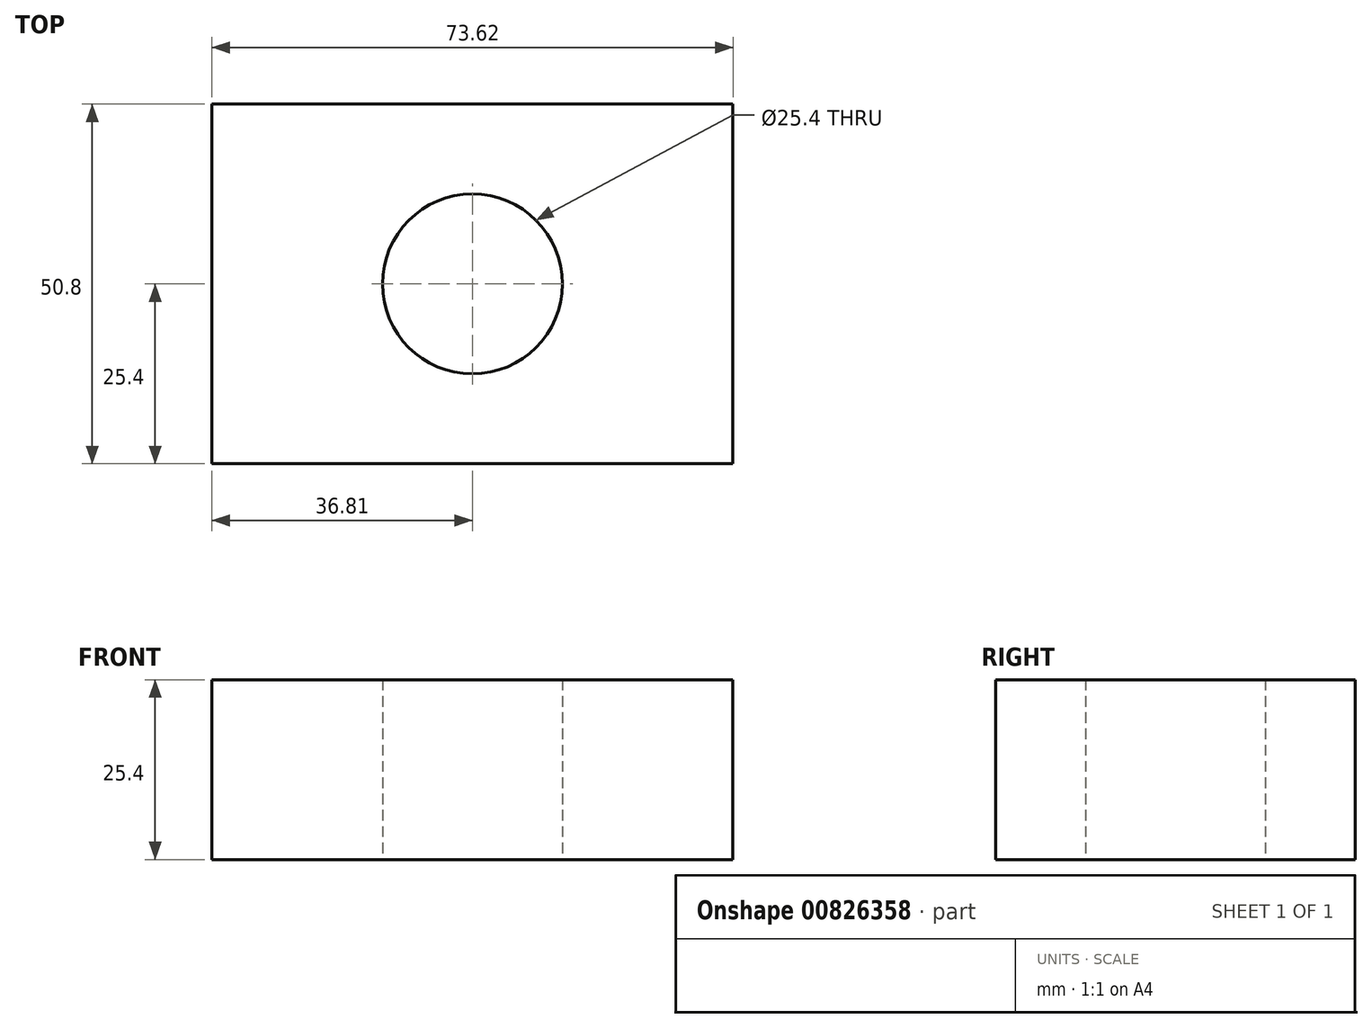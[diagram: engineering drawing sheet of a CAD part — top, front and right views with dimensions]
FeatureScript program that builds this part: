
annotation { "Feature Type Name" : "Feature", "Feature Type Description" : "" }
export const myFeature = defineFeature(function(context is Context, id is Id, definition is map)
    precondition{}
    {
        {
            var Q0;
            Q0=qCreatedBy(makeId("Top.planeOp"),FACE);
            var sketch = newSketch(context, id + "F0", { "sketchPlane" : qUnion([Q0])});
            skLineSegment(sketch, "E0.bottom", {"start": v(36.8, 25.4) * mm, "end": v(-36.8, 25.4) * mm});
            skLineSegment(sketch, "E0.top", {"start": v(36.8, -25.4) * mm, "end": v(-36.8, -25.4) * mm});
            skLineSegment(sketch, "E0.left", {"start": v(36.8, 25.4) * mm, "end": v(36.8, -25.4) * mm});
            skLineSegment(sketch, "E0.right", {"start": v(-36.8, 25.4) * mm, "end": v(-36.8, -25.4) * mm});
            skPoint(sketch, "E0.middle", {"position": v(0, 0) * mm});
            skCircle(sketch, "E1", {"center": v(0, 0) * mm, "radius": 12.7 * mm});
            skSolve(sketch);
        }
        {
            var Q0;
            Q0=makeQuery(id+"F0.imprint","IMPRINT",FACE,{"disambiguationData":[TD([[makeQuery(id+"F0.imprint","IMPRINT",EDGE,{"derivedFrom":sQuery(id+"F0.wireOp",EDGE,"E0.bottom")}),1.0]])]});
            extrude(context, id + "F1", {"entities" : qUnion([Q0]), "depth" : 25.4 * mm, "offsetDistance" : 25.4 * mm});
        }
    });
